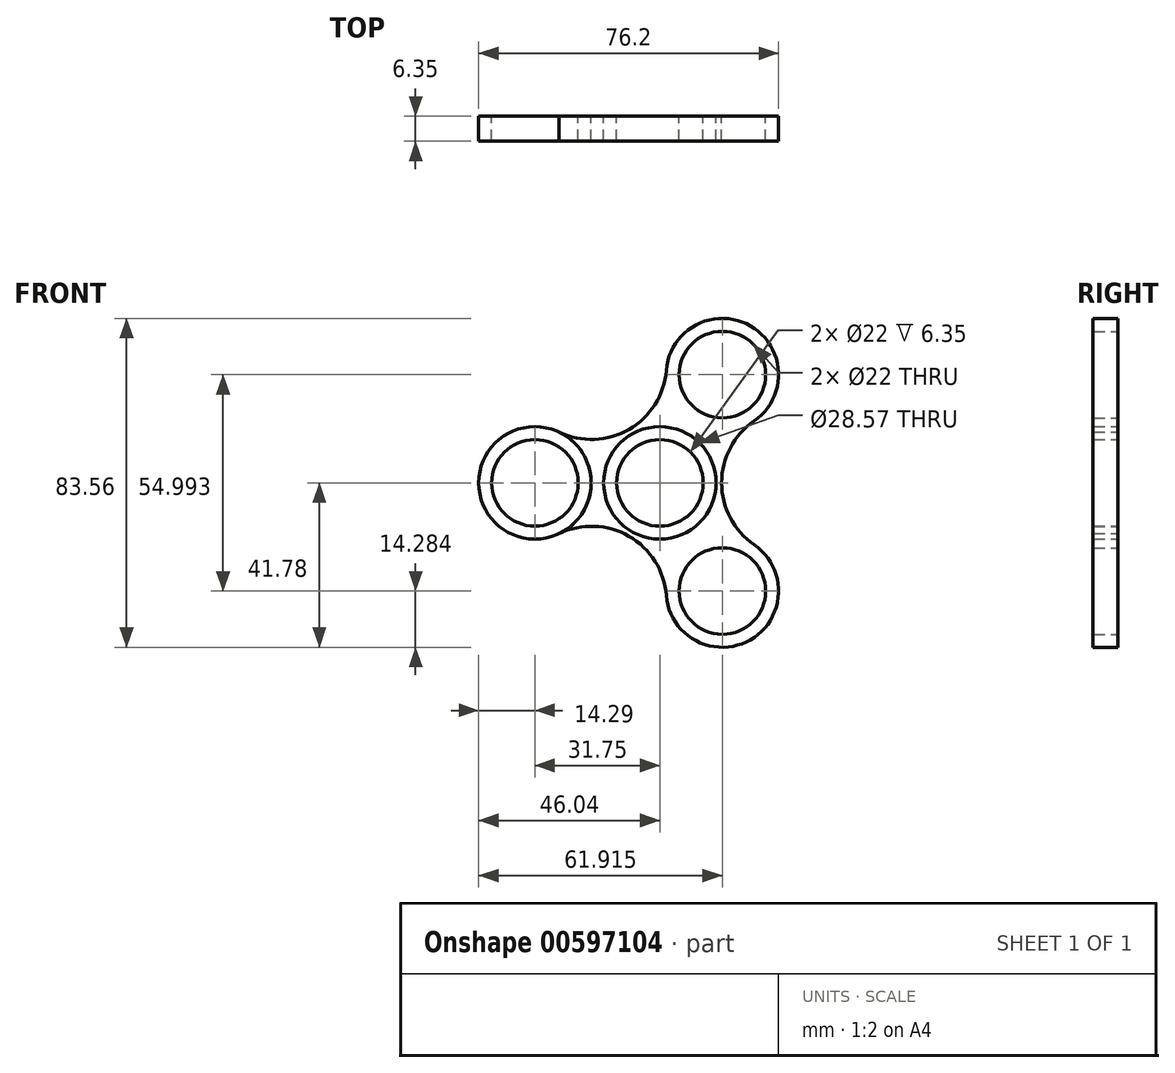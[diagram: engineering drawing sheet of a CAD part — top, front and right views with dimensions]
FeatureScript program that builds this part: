
annotation { "Feature Type Name" : "Feature", "Feature Type Description" : "" }
export const myFeature = defineFeature(function(context is Context, id is Id, definition is map)
    precondition{}
    {
        {
            var Q0;
            Q0=qCreatedBy(makeId("Front.planeOp"),FACE);
            var sketch = newSketch(context, id + "F0", { "sketchPlane" : qUnion([Q0])});
            skCircle(sketch, "E0", {"center": v(0, 0) * mm, "radius": 14.29 * mm});
            skCircle(sketch, "E1", {"center": v(0, 0) * mm, "radius": 11 * mm});
            skCircle(sketch, "E2", {"center": v(-31.75, 0) * mm, "radius": 14.29 * mm});
            skCircle(sketch, "E3", {"center": v(-31.75, 0) * mm, "radius": 11 * mm});
            skCircle(sketch, "E4.1.0", {"center": v(15.87, -27.5) * mm, "radius": 11 * mm});
            skCircle(sketch, "E4.1.1", {"center": v(15.87, -27.5) * mm, "radius": 14.29 * mm});
            skCircle(sketch, "E4.2.0", {"center": v(15.88, 27.5) * mm, "radius": 11 * mm});
            skCircle(sketch, "E4.2.1", {"center": v(15.88, 27.5) * mm, "radius": 14.29 * mm});
            skSolve(sketch);
        }
        {
            var Q0;
            Q0=qCreatedBy(makeId("Front.planeOp"),FACE);
            var sketch = newSketch(context, id + "F1", { "sketchPlane" : qUnion([Q0])});
            skArc(sketch, "E5", {"start": v(-25.58, 12.89) * mm, "mid": v(-7.84, 13.58) * mm, "end": v(1.63, 28.6) * mm});
            skArc(sketch, "E6", {"start": v(23.95, 15.71) * mm, "mid": v(15.68, 0) * mm, "end": v(23.95, -15.71) * mm});
            skArc(sketch, "E7", {"start": v(1.63, -28.6) * mm, "mid": v(-7.84, -13.58) * mm, "end": v(-25.58, -12.89) * mm});
            skCircle(sketch, "E8.0", {"center": v(-31.75, 0) * mm, "radius": 11 * mm});
            skCircle(sketch, "E9.0", {"center": v(-31.75, 0) * mm, "radius": 14.29 * mm});
            skCircle(sketch, "E10.0", {"center": v(0, 0) * mm, "radius": 14.29 * mm});
            skCircle(sketch, "E11.0", {"center": v(0, 0) * mm, "radius": 11 * mm});
            skCircle(sketch, "E12.0", {"center": v(15.88, 27.5) * mm, "radius": 14.29 * mm});
            skCircle(sketch, "E13.0", {"center": v(15.88, 27.5) * mm, "radius": 11 * mm});
            skCircle(sketch, "E14.0", {"center": v(15.87, -27.5) * mm, "radius": 14.29 * mm});
            skCircle(sketch, "E15.0", {"center": v(15.87, -27.5) * mm, "radius": 11 * mm});
            skSolve(sketch);
        }
        {
            var Q0;
            Q0=makeQuery(id+"F1.imprint","IMPRINT",FACE,{"disambiguationData":[TD([[makeQuery(id+"F1.imprint","IMPRINT",EDGE,{"derivedFrom":sQuery(id+"F1.wireOp",EDGE,"E13.0")}),-1.0]])]});
            var Q1;
            {var subQ4=sQuery(id+"F1.wireOp",EDGE,"E5");Q1=makeQuery(id+"F1.imprint","IMPRINT",FACE,{"disambiguationData":[TD([[makeQuery(id+"F1.imprint","IMPRINT",EDGE,{"derivedFrom":subQ4}),-1.0]])]});}
            var Q2;
            Q2=makeQuery(id+"F0.imprint","IMPRINT",FACE,{"disambiguationData":[TD([[makeQuery(id+"F0.imprint","IMPRINT",EDGE,{"derivedFrom":sQuery(id+"F0.wireOp",EDGE,"E0")}),1.0]])]});
            var Q3;
            Q3=makeQuery(id+"F0.imprint","IMPRINT",FACE,{"disambiguationData":[TD([[makeQuery(id+"F0.imprint","IMPRINT",EDGE,{"derivedFrom":sQuery(id+"F0.wireOp",EDGE,"E2")}),1.0]])]});
            var Q4;
            Q4=makeQuery(id+"F1.imprint","IMPRINT",FACE,{"disambiguationData":[TD([[makeQuery(id+"F1.imprint","IMPRINT",EDGE,{"derivedFrom":sQuery(id+"F1.wireOp",EDGE,"E15.0")}),-1.0]])]});
            extrude(context, id + "F2", {"entities" : qUnion([Q0, Q1, Q2, Q3, Q4]), "depth" : 6.35 * mm, "offsetDistance" : 25.4 * mm});
        }
    });
